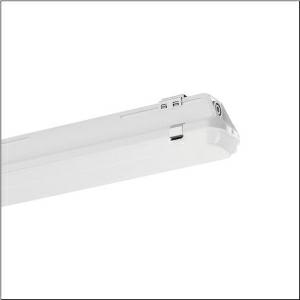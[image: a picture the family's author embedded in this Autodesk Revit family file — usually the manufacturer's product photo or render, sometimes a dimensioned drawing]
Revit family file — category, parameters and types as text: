
# Revit family: monsun_r__21_51fb10dp360b_a0ac
name_source: partatom
category: Lighting Fixtures
units: mm (PartAtom-declared; Revit-internal decimal feet)

## family parameters
Cut with Voids When Loaded = No
Host = Face
Light Source = No
Part Type = Normal
Room Calculation Point = No
Round Connector Dimension = Use Diameter
Shared = No

## types (1)
- --- (1 x LED, 6060 lm, 43.2 W, 3000K)
    Apparent Load = 43 VA
    CIE Flux Codes = 47 77 93 94 100
    Color Rendering = 80
    Color Temperature = 3000K
    Default Elevation = 1800 mm
    Description = Monsun® 21, damp-proof luminaire, chain hanger, primary optical cover: enclosure, of PMMA, light emission: direct distribution, primary light characteristic: symmetric, installation type: suspended mounting, surface-mounted, horizontal mounting, vertical mounting, LED, rated luminous flux: 6.060lm, luminous efficacy: 154lm/W, light colour: 830, colour temperature: 3000K, control gear: DALI 2, with terminal, 5-pole, max. 2.5mm², mains connection: 220..240V, AC, 50/60Hz, rated input power: 39W, housing, of glass-fibre reinforced polyester, uncoated, bright grey, incl. chain hanger, length: 1.590mm, width: 90mm, height: 88mm, clip for enclosure, of stainless steel (V2A), ceiling mounting element, of stainless steel (V2A), chain hanger, of stainless steel (V2A), protection rating (complete): IP66, insulation class (complete): insulation class I (protective earthing), certification: CE, ENEC, VDE, UKCA, protection symbol: D, impact resistance: IK04, permissible operating ambient temperature: -25..+35°C, standard: EN 50419, EN 60598-2-1, corresponds to IFS (International Featured Standards) requirements for safety and quality in the food industry, for indoor or canopied outdoor use, no direct snow, no direct sun, no direct rain, contact your sales advisor before using the luminaires in applications with unclear chemical exposure, large temperature fluctuations or condensation-forming humidity, LABS conformity tested according to VDMA 24364:2018-05, packaging unit: 1 piece
    Height = 89 mm
    Lamp = 1 x LED
    Lamp Light Flux = 6060 lm
    Lamp Power = 43.2 W
    Lamp count = 1
    Length = 1590 mm
    Luminous efficacy = 140 lm/W
    Manufacturer = Siteco
    ModVariant = No
    Model = 51FB10DP360B
    Mounting Place = Ceiling
    Mounting Type = Surface mounted
    Number of Poles = 1
    OnlyDefault = Yes
    Power Factor = 1
    Product Name = Monsun® 21
    Product group = damp-proof luminaire
    ProductGroupID = 300
    Protection Class = Protection class I
    Protection Degree = IP 66
    RLX_Detail_Level = 1
    RLX_Emergency_Light_Flux = 0 lm
    RLX_Emergency_Type = 0
    RLX_Emergency_Type_DB = No
    RlxData = <blob elided: 92461 chars, md5=2f4ec256>
    Socket = socket
    Standby Power = 0 W
    System Light Flux = 6060 lm
    System Power = 43 W
    Type Comments = factory setting: luminous flux: 100 % | dim-lin: 254 | 286 mA
    Type Image = l_1319656.jpg
    URL = http://relux.com
    VarID = @adj_146784
    Voltage = 0 V
    Weight = 0.00 kg
    Width = 90 mm

## geometry (parser evidence)
native form markers: Blend x4, Sweep x14
no freeform markers — native parametric forms only
